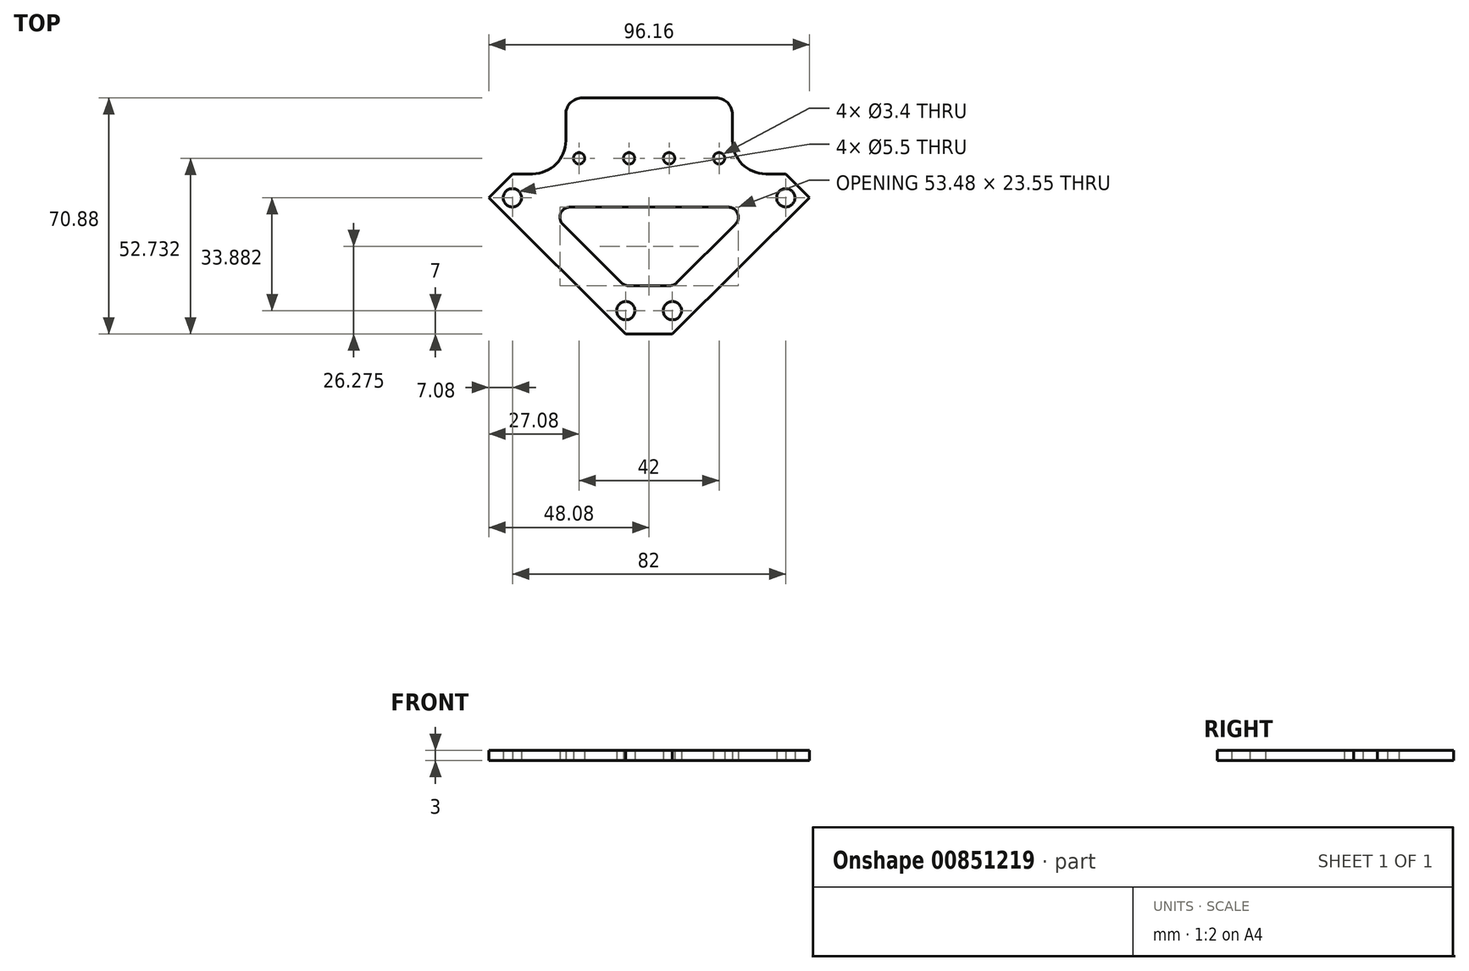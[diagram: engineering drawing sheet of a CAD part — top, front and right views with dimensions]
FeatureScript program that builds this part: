
annotation { "Feature Type Name" : "Feature", "Feature Type Description" : "" }
export const myFeature = defineFeature(function(context is Context, id is Id, definition is map)
    precondition{}
    {
        {
            var Q0;
            Q0=qCreatedBy(makeId("Top.planeOp"),FACE);
            var sketch = newSketch(context, id + "F0", { "sketchPlane" : qUnion([Q0])});
            skLineSegment(sketch, "E0", {"start": v(0, 48.05) * mm, "end": v(41, 48.05) * mm});
            skLineSegment(sketch, "E1", {"start": v(41, 48.05) * mm, "end": v(48.08, 40.94) * mm});
            skLineSegment(sketch, "E2", {"start": v(48.08, 40.94) * mm, "end": v(7, 0) * mm});
            skLineSegment(sketch, "E3", {"start": v(7, 0) * mm, "end": v(0, 0) * mm});
            skCircle(sketch, "E4", {"center": v(41, 40.88) * mm, "radius": 2.75 * mm});
            skCircle(sketch, "E5", {"center": v(7, 7) * mm, "radius": 2.75 * mm});
            skLineSegment(sketch, "E6", {"start": v(7, 7) * mm, "end": v(41, 40.88) * mm, "construction": true});
            skLineSegment(sketch, "E7", {"start": v(0, 0) * mm, "end": v(0, 48.05) * mm, "construction": true});
            skLineSegment(sketch, "E8.MirrorCS", {"start": v(-7, 0) * mm, "end": v(0, 0) * mm});
            skLineSegment(sketch, "E9.MirrorCS", {"start": v(-48.08, 40.94) * mm, "end": v(-7, 0) * mm});
            skLineSegment(sketch, "E10.MirrorCS", {"start": v(-41, 48.05) * mm, "end": v(-48.08, 40.94) * mm});
            skLineSegment(sketch, "E11.MirrorCS", {"start": v(-7, 7) * mm, "end": v(-41, 40.88) * mm, "construction": true});
            skLineSegment(sketch, "E12.MirrorCS", {"start": v(0, 48.05) * mm, "end": v(-41, 48.05) * mm});
            skCircle(sketch, "E13.MirrorC", {"center": v(-41, 40.88) * mm, "radius": 2.75 * mm});
            skCircle(sketch, "E14.MirrorC", {"center": v(-7, 7) * mm, "radius": 2.75 * mm});
            skSolve(sketch);
        }
        {
            var Q0;
            Q0=qCreatedBy(makeId("Top.planeOp"),FACE);
            var sketch = newSketch(context, id + "F1", { "sketchPlane" : qUnion([Q0])});
            skLineSegment(sketch, "E15.0", {"start": v(7, 0) * mm, "end": v(0, 0) * mm});
            skLineSegment(sketch, "E15.1", {"start": v(-7, 0) * mm, "end": v(0, 0) * mm});
            skLineSegment(sketch, "E15.2", {"start": v(-48.08, 40.94) * mm, "end": v(-7, 0) * mm});
            skLineSegment(sketch, "E15.3", {"start": v(48.08, 40.94) * mm, "end": v(7, 0) * mm});
            skLineSegment(sketch, "E15.4", {"start": v(35, 48.05) * mm, "end": v(41, 48.05) * mm});
            skLineSegment(sketch, "E15.5", {"start": v(41, 48.05) * mm, "end": v(48.08, 40.94) * mm});
            skLineSegment(sketch, "E15.6", {"start": v(-35, 48.05) * mm, "end": v(-41, 48.05) * mm});
            skLineSegment(sketch, "E15.7", {"start": v(-41, 48.05) * mm, "end": v(-48.08, 40.94) * mm});
            skCircle(sketch, "E16.0", {"center": v(-41, 40.88) * mm, "radius": 2.75 * mm});
            skCircle(sketch, "E16.1", {"center": v(-7, 7) * mm, "radius": 2.75 * mm});
            skCircle(sketch, "E16.2", {"center": v(7, 7) * mm, "radius": 2.75 * mm});
            skCircle(sketch, "E16.3", {"center": v(41, 40.88) * mm, "radius": 2.75 * mm});
            skLineSegment(sketch, "E17", {"start": v(25, 58.05) * mm, "end": v(25, 65.88) * mm});
            skLineSegment(sketch, "E18", {"start": v(20, 70.88) * mm, "end": v(0, 70.88) * mm});
            skPoint(sketch, "E19.newPointA", {"position": v(0, 48.05) * mm});
            skArc(sketch, "E19.filletArc", {"start": v(25, 58.05) * mm, "mid": v(27.93, 50.98) * mm, "end": v(35, 48.05) * mm});
            skCircle(sketch, "E20", {"center": v(21, 52.73) * mm, "radius": 1.7 * mm});
            skCircle(sketch, "E21", {"center": v(6, 52.73) * mm, "radius": 1.7 * mm});
            skPoint(sketch, "E22.visualSharp", {"position": v(25, 70.88) * mm});
            skArc(sketch, "E22.filletArc", {"start": v(25, 65.88) * mm, "mid": v(23.54, 69.42) * mm, "end": v(20, 70.88) * mm});
            skLineSegment(sketch, "E23", {"start": v(0, 14.5) * mm, "end": v(6.14, 14.5) * mm});
            skLineSegment(sketch, "E24", {"start": v(8.26, 15.38) * mm, "end": v(25.87, 32.92) * mm});
            skLineSegment(sketch, "E25", {"start": v(23.76, 38.05) * mm, "end": v(0, 38.05) * mm});
            skPoint(sketch, "E26.visualSharp", {"position": v(31.02, 38.05) * mm});
            skArc(sketch, "E26.filletArc", {"start": v(25.87, 32.92) * mm, "mid": v(26.53, 36.2) * mm, "end": v(23.76, 38.05) * mm});
            skPoint(sketch, "E27.visualSharp", {"position": v(7.38, 14.5) * mm});
            skArc(sketch, "E27.filletArc", {"start": v(6.14, 14.5) * mm, "mid": v(7.29, 14.73) * mm, "end": v(8.26, 15.38) * mm});
            skLineSegment(sketch, "E28.MirrorCS", {"start": v(-23.76, 38.05) * mm, "end": v(0, 38.05) * mm});
            skArc(sketch, "E29.MirrorCS", {"start": v(-25.87, 32.92) * mm, "mid": v(-26.53, 36.2) * mm, "end": v(-23.76, 38.05) * mm});
            skLineSegment(sketch, "E30.MirrorCS", {"start": v(-8.26, 15.38) * mm, "end": v(-25.87, 32.92) * mm});
            skArc(sketch, "E31.MirrorCS", {"start": v(-6.14, 14.5) * mm, "mid": v(-7.29, 14.73) * mm, "end": v(-8.26, 15.38) * mm});
            skLineSegment(sketch, "E32.MirrorCS", {"start": v(0, 14.5) * mm, "end": v(-6.14, 14.5) * mm});
            skLineSegment(sketch, "E33.MirrorCS", {"start": v(-20, 70.88) * mm, "end": v(0, 70.88) * mm});
            skArc(sketch, "E34.MirrorCS", {"start": v(-25, 65.88) * mm, "mid": v(-23.54, 69.42) * mm, "end": v(-20, 70.88) * mm});
            skLineSegment(sketch, "E35.MirrorCS", {"start": v(-25, 58.05) * mm, "end": v(-25, 65.88) * mm});
            skArc(sketch, "E36.MirrorCS", {"start": v(-25, 58.05) * mm, "mid": v(-27.93, 50.98) * mm, "end": v(-35, 48.05) * mm});
            skCircle(sketch, "E37.MirrorC", {"center": v(-6, 52.73) * mm, "radius": 1.7 * mm});
            skCircle(sketch, "E38.MirrorC", {"center": v(-21, 52.73) * mm, "radius": 1.7 * mm});
            skSolve(sketch);
        }
        {
            var Q0;
            Q0 = qSketchRegion(id + "F1", true);
            extrude(context, id + "F2", {"entities" : qUnion([Q0]), "depth" : 3 * mm, "offsetDistance" : 25 * mm});
        }
    });
